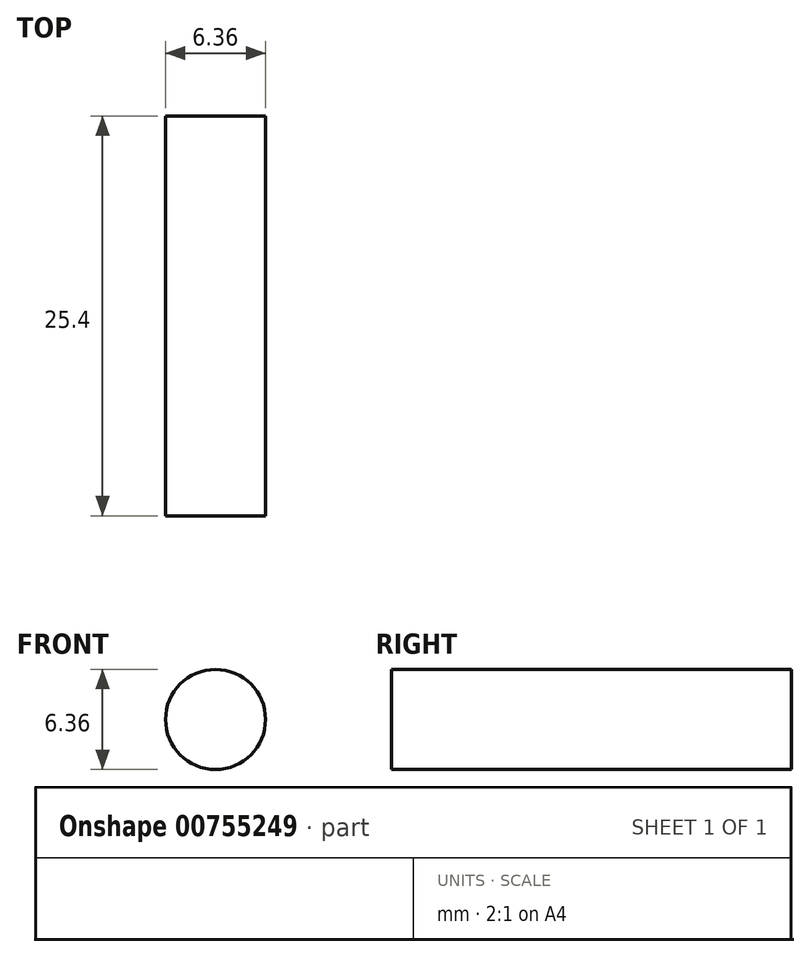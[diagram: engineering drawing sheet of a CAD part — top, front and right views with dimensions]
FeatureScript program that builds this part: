
annotation { "Feature Type Name" : "Feature", "Feature Type Description" : "" }
export const myFeature = defineFeature(function(context is Context, id is Id, definition is map)
    precondition{}
    {
        {
            var Q0;
            Q0=qCreatedBy(makeId("Front.planeOp"),FACE);
            var sketch = newSketch(context, id + "F0", { "sketchPlane" : qUnion([Q0])});
            skCircle(sketch, "E0", {"center": v(0, 0) * mm, "radius": 3.18 * mm});
            skSolve(sketch);
        }
        {
            var Q0;
            Q0=makeQuery(id+"F0.imprint","IMPRINT",FACE,{"disambiguationData":[TD([[makeQuery(id+"F0.imprint","IMPRINT",EDGE,{"derivedFrom":sQuery(id+"F0.wireOp",EDGE,"E0")}),1.0]])]});
            extrude(context, id + "F1", {"entities" : qUnion([Q0]), "depth" : 25.4 * mm, "offsetDistance" : 25.4 * mm});
        }
    });
